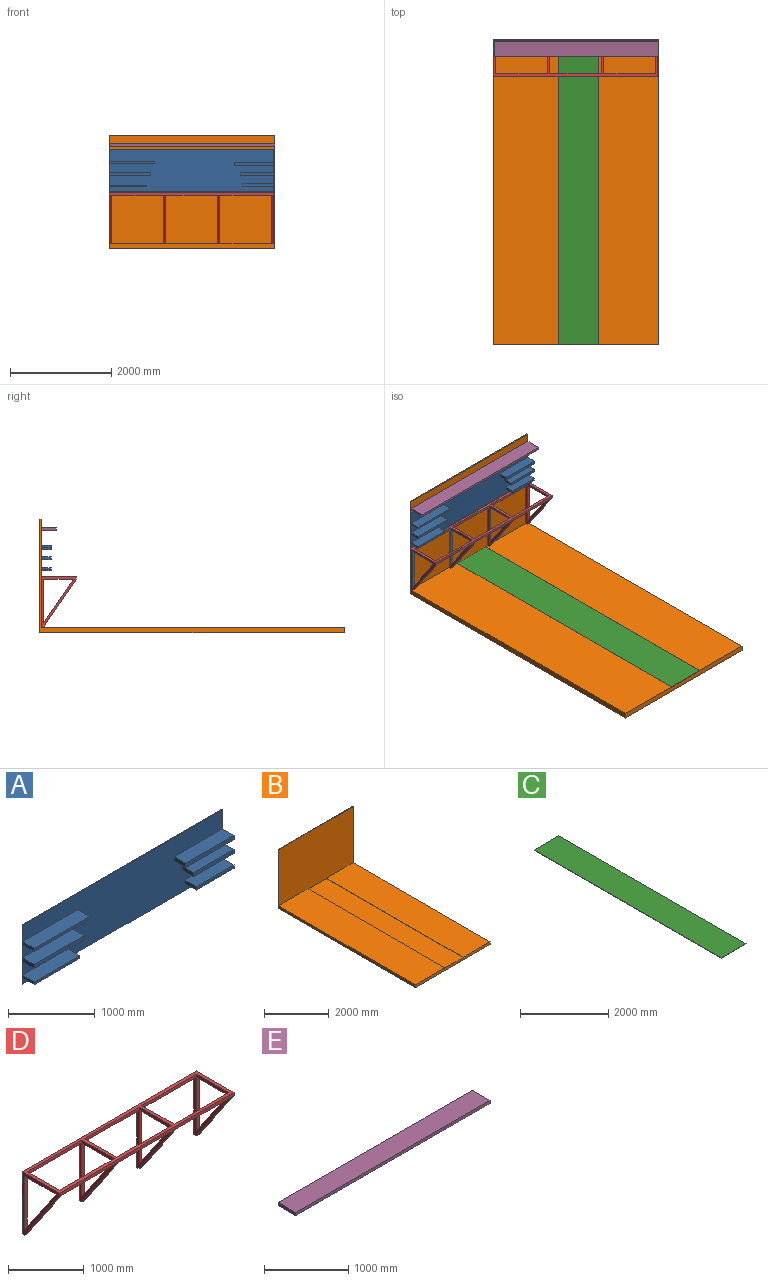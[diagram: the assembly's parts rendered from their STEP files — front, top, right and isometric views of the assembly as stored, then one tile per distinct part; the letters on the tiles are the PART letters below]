
ASSEMBLY  parts=5 mates=4
PART A: 30 faces, bbox 3260x200x833 mm
  f0: plane 3260x10mm, normal (0,0,-1), area 32600mm2, adj f1,f3,f4,f5
  f1: plane 832.95x200mm, normal (1,0,0), area 40270.1mm2, adj f0,f2,f4,f5,f18,f19,f21,f22
  f2: plane 3260x10mm, normal (0,0,1), area 32600mm2, adj f1,f3,f4,f5
  f3: plane 832.95x200mm, normal (-1,0,0), area 34136.3mm2, adj f0,f2,f4,f5,f6,f8,f9,f10
  f4: plane 3260x832.95mm, normal (0,-1,0), area 2487494.5mm2, adj f0,f1,f2,f3,f6,f7,f8,f10
  f5: plane 3260x832.95mm, normal (0,1,0), area 2715422.8mm2, adj f0,f1,f2,f3
  f6: plane 814.67x190mm, normal (0,0,-1), area 154788mm2, adj f3,f4,f7,f9
  f7: plane 190x56.99mm, normal (1,0,0), area 10827.4mm2, adj f4,f6,f8,f9
  f8: plane 814.67x190mm, normal (0,0,1), area 154788mm2, adj f3,f4,f7,f9
  f9: plane 814.67x56.99mm, normal (0,-1,0), area 46425.5mm2, adj f3,f6,f7,f8
  f10: plane 902.27x190mm, normal (0,0,-1), area 171431.6mm2, adj f3,f4,f11,f13
  f11: plane 190x41.33mm, normal (1,0,0), area 7852.2mm2, adj f4,f10,f12,f13
  f12: plane 902.27x190mm, normal (0,0,1), area 171431.6mm2, adj f3,f4,f11,f13
  f13: plane 902.27x41.33mm, normal (0,-1,0), area 37288.6mm2, adj f3,f10,f11,f12
  f14: plane 741.29x190mm, normal (0,0,-1), area 140844.5mm2, adj f3,f4,f15,f17
  f15: plane 190x37.51mm, normal (1,0,0), area 7127.2mm2, adj f4,f14,f16,f17
  f16: plane 741.29x190mm, normal (0,0,1), area 140844.5mm2, adj f3,f4,f15,f17
  f17: plane 741.29x37.51mm, normal (0,-1,0), area 27806.7mm2, adj f3,f14,f15,f16
  f18: plane 787.28x190mm, normal (0,0,-1), area 149582.8mm2, adj f1,f4,f20,f21
  f19: plane 787.28x190mm, normal (0,0,1), area 149582.8mm2, adj f1,f4,f20,f21
  f20: plane 190x62.06mm, normal (-1,0,0), area 11791.3mm2, adj f4,f18,f19,f21
  f21: plane 787.28x62.06mm, normal (0,-1,0), area 48858.2mm2, adj f1,f18,f19,f20
  f22: plane 656.65x190mm, normal (0,0,-1), area 124763.5mm2, adj f1,f4,f24,f25
  f23: plane 656.65x190mm, normal (0,0,1), area 124763.5mm2, adj f1,f4,f24,f25
  f24: plane 190x57.7mm, normal (-1,0,0), area 10963.8mm2, adj f4,f22,f23,f25
  f25: plane 656.65x57.7mm, normal (0,-1,0), area 37891.4mm2, adj f1,f22,f23,f24
  f26: plane 613.47x190mm, normal (0,0,-1), area 116559.2mm2, adj f1,f4,f28,f29
  f27: plane 613.47x190mm, normal (0,0,1), area 116559.2mm2, adj f1,f4,f28,f29
  f28: plane 190x48.34mm, normal (-1,0,0), area 9185.5mm2, adj f4,f26,f27,f29
  f29: plane 613.47x48.34mm, normal (0,-1,0), area 29658mm2, adj f1,f26,f27,f28
PART B: 12 faces, bbox 3270x6025x2240.3 mm
  f0: plane 6000x800mm, normal (0,0,1), area 4800000mm2, adj f2,f5,f7,f9
  f1: plane 6025x2240.29mm, normal (-1,0,0), area 716007.3mm2, adj f2,f4,f6,f9,f10,f11
  f2: plane 3270x110mm, normal (0,-1,0), area 351700mm2, adj f0,f1,f3,f4,f5,f6,f7,f8
  f3: plane 6025x2240.29mm, normal (1,0,0), area 716007.3mm2, adj f2,f4,f8,f9,f10,f11
  f4: plane 6025x3270mm, normal (0,0,-1), area 19701750mm2, adj f1,f2,f3,f11
  f5: plane 6000x10mm, normal (1,0,0), area 60000mm2, adj f0,f2,f6,f9
  f6: plane 6000x1290mm, normal (0,0,1), area 7740000mm2, adj f1,f2,f5,f9
  f7: plane 6000x10mm, normal (-1,0,0), area 60000mm2, adj f0,f2,f8,f9
  f8: plane 6000x1180mm, normal (0,0,1), area 7080000mm2, adj f2,f3,f7,f9
  f9: plane 3270x2140.29mm, normal (0,-1,0), area 6974054.6mm2, adj f0,f1,f3,f5,f6,f7,f8,f10
  f10: plane 3270x25mm, normal (0,0,1), area 81750mm2, adj f1,f3,f9,f11
  f11: plane 3270x2240.29mm, normal (0,1,0), area 7325754.6mm2, adj f1,f3,f4,f10
PART C: 6 faces, bbox 800x6000x10 mm
  f0: plane 800x10mm, normal (0,1,0), area 8000mm2, adj f1,f3,f4,f5
  f1: plane 6000x10mm, normal (-1,0,0), area 60000mm2, adj f0,f2,f4,f5
  f2: plane 800x10mm, normal (0,-1,0), area 8000mm2, adj f1,f3,f4,f5
  f3: plane 6000x10mm, normal (1,0,0), area 60000mm2, adj f0,f2,f4,f5
  f4: plane 6000x800mm, normal (0,0,1), area 4800000mm2, adj f0,f1,f2,f3
  f5: plane 6000x800mm, normal (0,0,-1), area 4800000mm2, adj f0,f1,f2,f3
PART D: 43 faces, bbox 3260x700x1000 mm
  f0: plane 950x650mm, normal (0,-0.83,-0.56), area 57554.3mm2, adj f1,f7,f8,f9
  f1: plane 50x50mm, normal (0,0,-1), area 2500mm2, adj f0,f2,f8,f9
  f2: plane 3260x1000mm, normal (0,1,0), area 353000mm2, adj f1,f3,f8,f9,f10,f11,f13,f20
  f3: plane 3260x700mm, normal (0,0,1), area 446000mm2, adj f2,f7,f8,f9,f10,f11,f18,f19
  f4: plane 861.46x50mm, normal (0,-1,0), area 43072.7mm2, adj f5,f6,f8,f9
  f5: plane 861.46x589.42mm, normal (0,0.83,0.56), area 52189.9mm2, adj f4,f6,f8,f9
  f6: plane 589.42x50mm, normal (0,0,-1), area 29470.8mm2, adj f4,f5,f8,f9
  f7: plane 3260x50mm, normal (0,-1,0), area 163000mm2, adj f0,f3,f8,f12,f17,f21,f27,f29
  f8: plane 1000x700mm, normal (-1,0,0), area 137372.1mm2, adj f0,f1,f2,f3,f4,f5,f6,f7
  f9: plane 1000x700mm, normal (1,0,0), area 132372.1mm2, adj f0,f1,f2,f3,f4,f5,f6,f39
  f10: plane 1000x700mm, normal (-1,0,0), area 132372.1mm2, adj f2,f3,f12,f13,f14,f15,f16,f39
  f11: plane 1000x700mm, normal (1,0,0), area 132372.1mm2, adj f2,f3,f12,f13,f14,f15,f16,f17
  f12: plane 950x650mm, normal (0,-0.83,-0.56), area 57554.3mm2, adj f7,f10,f11,f13
  f13: plane 50x50mm, normal (0,0,-1), area 2500mm2, adj f2,f10,f11,f12
  f14: plane 861.46x50mm, normal (0,-1,0), area 43072.7mm2, adj f10,f11,f15,f16
  f15: plane 861.46x589.42mm, normal (0,0.83,0.56), area 52189.9mm2, adj f10,f11,f14,f16
  f16: plane 589.42x50mm, normal (0,0,-1), area 29470.8mm2, adj f10,f11,f14,f15
  f17: plane 1020x50mm, normal (0,0,-1), area 51000mm2, adj f7,f11,f18,f38
  f18: plane 1020x50mm, normal (0,1,0), area 51000mm2, adj f3,f11,f17,f38
  f19: plane 1020x50mm, normal (0,-1,0), area 51000mm2, adj f3,f11,f20,f38
  f20: plane 1020x50mm, normal (0,0,-1), area 51000mm2, adj f2,f11,f19,f38
  f21: plane 950x650mm, normal (0,-0.83,-0.56), area 57554.3mm2, adj f7,f22,f26,f27
  f22: plane 50x50mm, normal (0,0,-1), area 2500mm2, adj f2,f21,f26,f27
  f23: plane 861.46x50mm, normal (0,-1,0), area 43072.7mm2, adj f24,f25,f26,f27
  f24: plane 861.46x589.42mm, normal (0,0.83,0.56), area 52189.9mm2, adj f23,f25,f26,f27
  f25: plane 589.42x50mm, normal (0,0,-1), area 29470.8mm2, adj f23,f24,f26,f27
  f26: plane 1000x700mm, normal (-1,0,0), area 132372.1mm2, adj f2,f3,f21,f22,f23,f24,f25,f28
  f27: plane 1000x700mm, normal (1,0,0), area 137372.1mm2, adj f2,f3,f7,f21,f22,f23,f24,f25
  f28: plane 1020x50mm, normal (0,1,0), area 51000mm2, adj f3,f26,f29,f37
  f29: plane 1020x50mm, normal (0,0,-1), area 51000mm2, adj f7,f26,f28,f37
  f30: plane 1020x50mm, normal (0,-1,0), area 51000mm2, adj f3,f26,f31,f37
  f31: plane 1020x50mm, normal (0,0,-1), area 51000mm2, adj f2,f26,f30,f37
  f32: plane 589.42x50mm, normal (0,0,-1), area 29470.8mm2, adj f33,f34,f37,f38
  f33: plane 861.46x589.42mm, normal (0,0.83,0.56), area 52189.9mm2, adj f32,f34,f37,f38
  f34: plane 861.46x50mm, normal (0,-1,0), area 43072.7mm2, adj f32,f33,f37,f38
  f35: plane 50x50mm, normal (0,0,-1), area 2500mm2, adj f2,f36,f37,f38
  f36: plane 950x650mm, normal (0,-0.83,-0.56), area 57554.3mm2, adj f7,f35,f37,f38
  f37: plane 1000x700mm, normal (1,0,0), area 132372.1mm2, adj f2,f3,f28,f29,f30,f31,f32,f33
  f38: plane 1000x700mm, normal (-1,0,0), area 132372.1mm2, adj f2,f3,f17,f18,f19,f20,f32,f33
  f39: plane 1020x50mm, normal (0,0,-1), area 51000mm2, adj f7,f9,f10,f40
  f40: plane 1020x50mm, normal (0,1,0), area 51000mm2, adj f3,f9,f10,f39
  f41: plane 1020x50mm, normal (0,0,-1), area 51000mm2, adj f2,f9,f10,f42
  f42: plane 1020x50mm, normal (0,-1,0), area 51000mm2, adj f3,f9,f10,f41
PART E: 6 faces, bbox 3260x300x44.5 mm
  f0: plane 300x44.47mm, normal (-1,0,0), area 13342.4mm2, adj f1,f3,f4,f5
  f1: plane 3260x300mm, normal (0,0,-1), area 978000mm2, adj f0,f2,f4,f5
  f2: plane 300x44.47mm, normal (1,0,0), area 13342.4mm2, adj f1,f3,f4,f5
  f3: plane 3260x300mm, normal (0,0,1), area 978000mm2, adj f0,f2,f4,f5
  f4: plane 3260x44.47mm, normal (0,-1,0), area 144987.2mm2, adj f0,f1,f2,f3
  f5: plane 3260x44.47mm, normal (0,1,0), area 144987.2mm2, adj f0,f1,f2,f3
PLACE A t=(-1584.51,2987.5,48.04)mm
PLACE B t=(0,2987.5,100)mm
PLACE C t=(0,2987.5,100)mm
PLACE D t=(-1585,2987.5,110)mm
PLACE E t=(-1568.36,2987.5,-23.36)mm
MATE planar A.f5 <-> B.f9  axis (0,1,0) through (-4.51,2987.5,1549.9)mm
MATE fastened B.f6 <-> D.f1  axis (0,0,1) through (-1635,2987.5,110)mm
MATE fastened B.f0 <-> C.f5  axis (0,0,1) through (455,2987.5,100)mm
MATE planar E.f5 <-> B.f9  axis (0,1,0) through (11.64,2987.5,2049.36)mm
